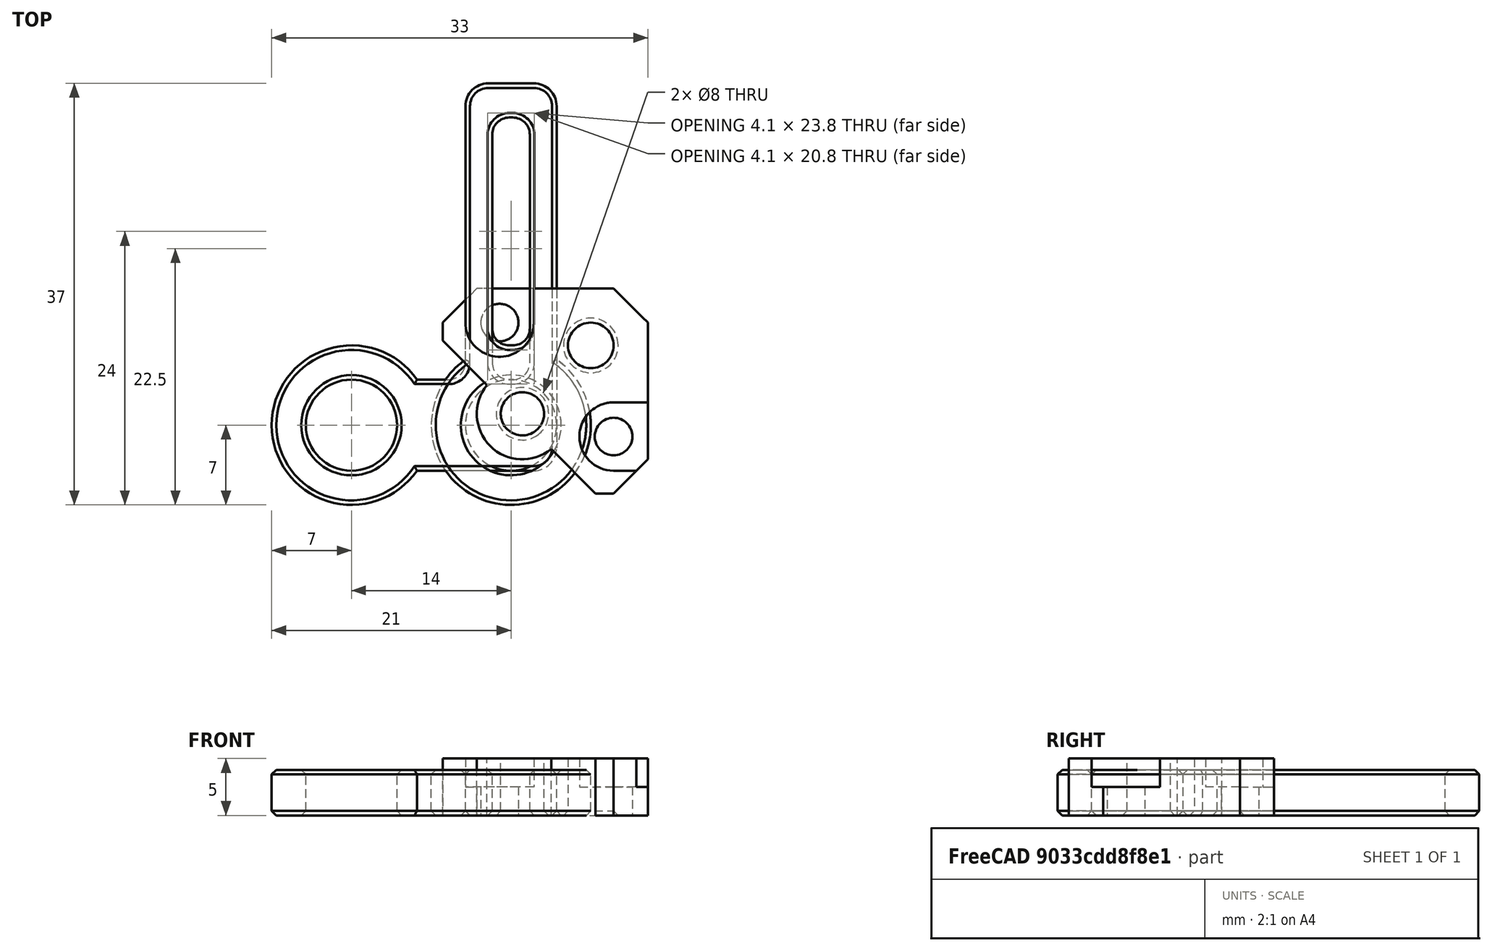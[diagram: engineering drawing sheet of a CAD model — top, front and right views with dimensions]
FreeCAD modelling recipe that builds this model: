
FCSTD DOCUMENT  (FreeCAD 0.19R24291 (Git))
Label: ptfe-tube-router
License: Other
LicenseURL: GPL3
objects: Part::Box×6, Part::Fillet×5, Part::Chamfer×5, Part::Cut×4, Part::MultiFuse×4, Part::Feature×2, Part::FeaturePython×2, Part::Cylinder×2, Part::Refine×2
note: 32 computed .brp shape members not serialized (recipe doc carries the construction recipe); baked Part::Feature solids carry a one-line shape summary decoded from their .brp

FEATURE [Part::Feature] Cut002008023012009006003002007002  label="corner-mount"
  Placement = pos=(0,0,5) rot=(0,1,0;3.14159rad)
  shape: bbox 18 x 18 x 6 mm, 23 faces (baked)
FEATURE [Part::Box] Box  label="Cube"
  AttacherType = Attacher::AttachEngine3D
  Height = 10
  Length = 10
  Placement = pos=(1.5,1.5,5) rot=(0,0,1;0rad)
  Width = 10
FEATURE [Part::Cut] Cut
  Base = -> Cut002008023012009006003002007002
  Tool = -> Box
FEATURE [Part::FeaturePython] Tube  # WARN: FeaturePython — macro-defined, semantics opaque (R4)
  AttacherType = Attacher::AttachEngine3D
  Height = 4
  InnerRadius = 4
  OuterRadius = 7
FEATURE [Part::Box] Box001001002  label="Cube004"
  AttacherType = Attacher::AttachEngine3D
  Height = 10
  Length = 3.3
  Placement = pos=(-1.65,7,0) rot=(0,0,1;0rad)
  Width = 20
FEATURE [Part::Box] Box001001003  label="Cube005"
  AttacherType = Attacher::AttachEngine3D
  Height = 4
  Length = 8
  Placement = pos=(-4,5,0) rot=(0,0,1;0rad)
  Width = 25
FEATURE [Part::Fillet] Fillet001
  Base = -> Box001001002
  Edges = 4 edges r=1.5: [Edge1,Edge3,Edge5,Edge7]
FEATURE [Part::Fillet] Fillet002
  Base = -> Box001001003
  Edges = 2 edges r=2: [Edge3,Edge7]
FEATURE [Part::Cut] Cut002008023012009006003002007003
  Base = -> Fillet002
  Tool = -> Fillet001
FEATURE [Part::Chamfer] Chamfer001
  Base = -> Tube
  Edges = 4 edges r=0.4: [Edge1,Edge3,Edge4,Edge5]
FEATURE [Part::Chamfer] Chamfer002
  Base = -> Cut002008023012009006003002007003
  Edges = 28 edges r=0.4: [Edge1,Edge3,Edge5,Edge6,Edge7,Edge8,Edge9,Edge10,Edge11,Edge12,Edge13,Edge14,Edge15,Edge16,Edge17,Edge18,Edge20,Edge21,Edge22,Edge23,Edge24,Edge25,Edge26,Edge27,Edge28,Edge29,Edge30,Edge31]
FEATURE [Part::MultiFuse] Fusion001  label="ptfe-tube-guide-arm-straight"
  Shapes = -> [Chamfer001,Chamfer002]
FEATURE [Part::Cylinder] Cylinder
  Angle = 360
  AttacherType = Attacher::AttachEngine3D
  Height = 5
  Placement = pos=(1,1,0) rot=(0,0,1;0rad)
  Radius = 4
FEATURE [Part::Cylinder] Cylinder001
  Angle = 360
  AttacherType = Attacher::AttachEngine3D
  Height = 5
  Placement = pos=(1,1,0) rot=(0,0,1;0rad)
  Radius = 1.9
FEATURE [Part::MultiFuse] Fusion
  Shapes = -> [Cylinder,Cut]
FEATURE [Part::Cut] Cut002008023012009006003002007004
  Base = -> Fusion
  Tool = -> Cylinder001
FEATURE [Part::Chamfer] Chamfer  label="ptfe-tube-guide-base"
  Base = -> Cut002008023012009006003002007004
  Edges = 4 edges r=0.4: [Edge2,Edge3,Edge8,Edge25]
FEATURE [Part::Box] Box001001004  label="Cube006"
  AttacherType = Attacher::AttachEngine3D
  Height = 10
  Length = 3.3
  Placement = pos=(-1.65,4,0) rot=(0,0,1;0rad)
  Width = 23
FEATURE [Part::Box] Box001001005  label="Cube007"
  AttacherType = Attacher::AttachEngine3D
  Height = 4
  Length = 8
  Placement = pos=(-4,-4,0) rot=(0,0,1;0rad)
  Width = 34
FEATURE [Part::FeaturePython] Tube001  # WARN: FeaturePython — macro-defined, semantics opaque (R4)
  AttacherType = Attacher::AttachEngine3D
  Height = 4
  InnerRadius = 4
  OuterRadius = 7
FEATURE [Part::Chamfer] Chamfer004
  Base = -> Tube001
  Edges = 4 edges r=0.4: [Edge1,Edge3,Edge4,Edge5]
  Placement = pos=(-14,0,0) rot=(0,0,1;0rad)
FEATURE [Part::Box] Box001001006  label="Cube008"
  AttacherType = Attacher::AttachEngine3D
  Height = 4
  Length = 8
  Placement = pos=(-9,-4,0) rot=(0,0,1;0rad)
  Width = 8
FEATURE [Part::MultiFuse] Fusion002
  Shapes = -> [Box001001006,Box001001005]
FEATURE [Part::Fillet] Fillet
  Base = -> Fusion002
  Edges = 3 edges r=2: [Edge19,Edge24,Edge29]
FEATURE [Part::Fillet] Fillet003
  Base = -> Box001001004
  Edges = 4 edges r=1.5: [Edge1,Edge3,Edge5,Edge7]
FEATURE [Part::Fillet] Fillet004
  Base = -> Fillet
  Edges = 1 edges r=1.5: [Edge2]
FEATURE [Part::Cut] Cut002008023012009006003002007005
  Base = -> Fillet004
  Tool = -> Fillet003
FEATURE [Part::Refine] Cut002008023012009006003002007005001
  Source = -> Cut002008023012009006003002007005
FEATURE [Part::Chamfer] Chamfer005
  Base = -> Cut002008023012009006003002007005001
  Edges = 36 edges r=0.4: [Edge1,Edge3,Edge5,Edge7,Edge8,Edge10,Edge11,Edge12,Edge14,Edge16,Edge17,Edge19,Edge20,Edge21,Edge23,Edge25,Edge27,Edge28,Edge29,Edge30,Edge31,Edge32,Edge33,Edge34,Edge35,Edge36,Edge37,Edge40,Edge41,Edge44,Edge46,Edge48,Edge49,Edge52,Edge53,Edge54]
FEATURE [Part::MultiFuse] Fusion003
  Shapes = -> [Chamfer004,Chamfer005]
FEATURE [Part::Refine] Fusion003001
  Source = -> Fusion003
FEATURE [Part::Feature] Fusion003001001
  shape: bbox 25 x 37 x 4 mm, 59 faces (baked)
